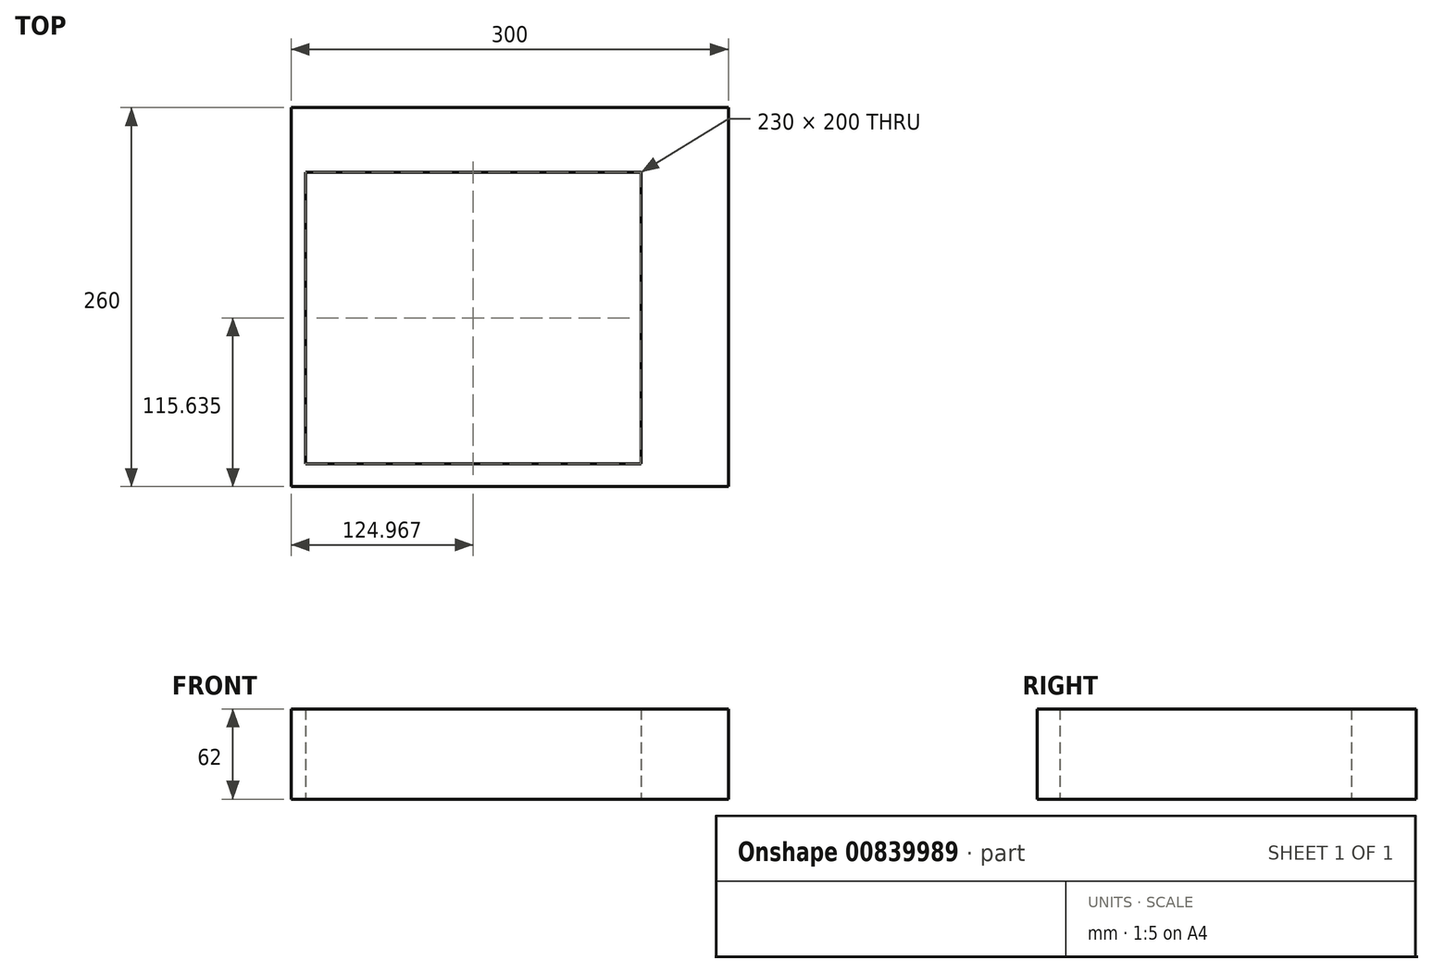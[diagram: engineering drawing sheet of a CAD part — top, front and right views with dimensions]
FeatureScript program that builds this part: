
annotation { "Feature Type Name" : "Feature", "Feature Type Description" : "" }
export const myFeature = defineFeature(function(context is Context, id is Id, definition is map)
    precondition{}
    {
        {
            var Q0;
            Q0=qCreatedBy(makeId("Top.planeOp"),FACE);
            var sketch = newSketch(context, id + "F0", { "sketchPlane" : qUnion([Q0])});
            skLineSegment(sketch, "E0.bottom", {"start": v(0, 0) * mm, "end": v(300, 0) * mm});
            skLineSegment(sketch, "E0.top", {"start": v(0, 260) * mm, "end": v(300, 260) * mm});
            skLineSegment(sketch, "E0.left", {"start": v(0, 0) * mm, "end": v(0, 260) * mm});
            skLineSegment(sketch, "E0.right", {"start": v(300, 0) * mm, "end": v(300, 260) * mm});
            skLineSegment(sketch, "E1.bottom", {"start": v(9.97, 215.64) * mm, "end": v(239.97, 215.64) * mm});
            skLineSegment(sketch, "E1.top", {"start": v(9.97, 15.64) * mm, "end": v(239.97, 15.64) * mm});
            skLineSegment(sketch, "E1.left", {"start": v(9.97, 215.64) * mm, "end": v(9.97, 15.64) * mm});
            skLineSegment(sketch, "E1.right", {"start": v(239.97, 215.64) * mm, "end": v(239.97, 15.64) * mm});
            skSolve(sketch);
        }
        {
            var Q0;
            Q0=makeQuery(id+"F0.imprint","IMPRINT",FACE,{"disambiguationData":[TD([[makeQuery(id+"F0.imprint","IMPRINT",EDGE,{"derivedFrom":sQuery(id+"F0.wireOp",EDGE,"E0.bottom")}),1.0]])]});
            extrude(context, id + "F1", {"entities" : qUnion([Q0]), "depth" : 62 * mm, "offsetDistance" : 25 * mm});
        }
    });
